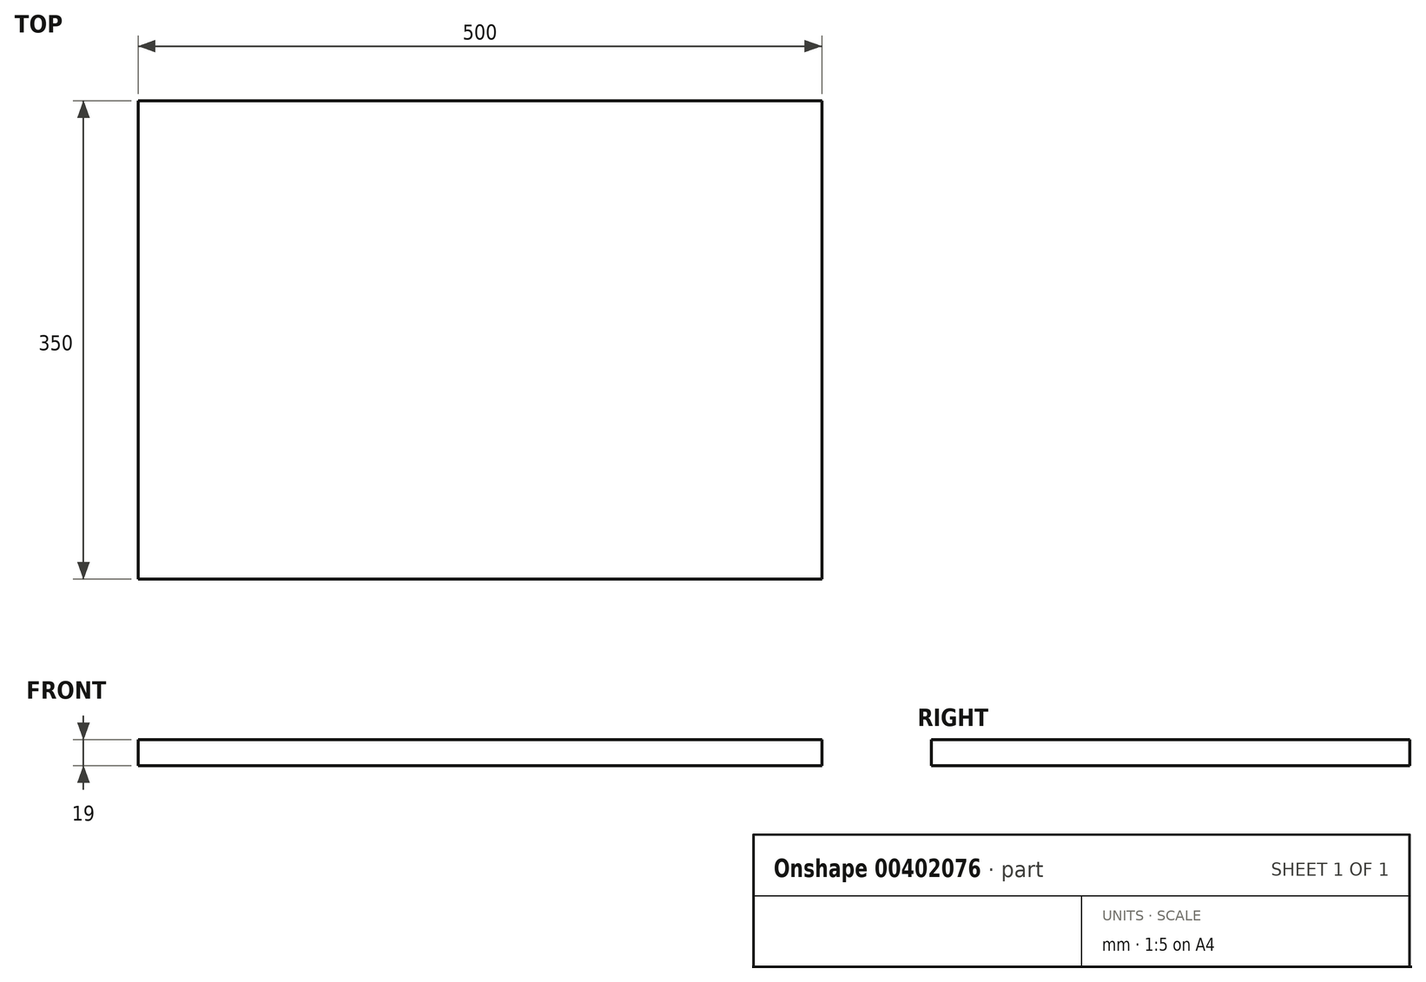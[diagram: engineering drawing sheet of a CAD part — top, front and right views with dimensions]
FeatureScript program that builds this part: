
annotation { "Feature Type Name" : "Feature", "Feature Type Description" : "" }
export const myFeature = defineFeature(function(context is Context, id is Id, definition is map)
    precondition{}
    {
        {
            var Q0;
            Q0=qCreatedBy(makeId("Top.planeOp"),FACE);
            var sketch = newSketch(context, id + "F0", { "sketchPlane" : qUnion([Q0])});
            skLineSegment(sketch, "E0.bottom", {"start": v(0, 0) * mm, "end": v(500, 0) * mm});
            skLineSegment(sketch, "E0.top", {"start": v(0, 350) * mm, "end": v(500, 350) * mm});
            skLineSegment(sketch, "E0.left", {"start": v(0, 0) * mm, "end": v(0, 350) * mm});
            skLineSegment(sketch, "E0.right", {"start": v(500, 0) * mm, "end": v(500, 350) * mm});
            skSolve(sketch);
        }
        {
            var Q0;
            Q0=qSketchRegion(id+"F0",true);
            extrude(context, id + "F1", {"entities" : qUnion([Q0]), "depth" : 19 * mm});
        }
    });
